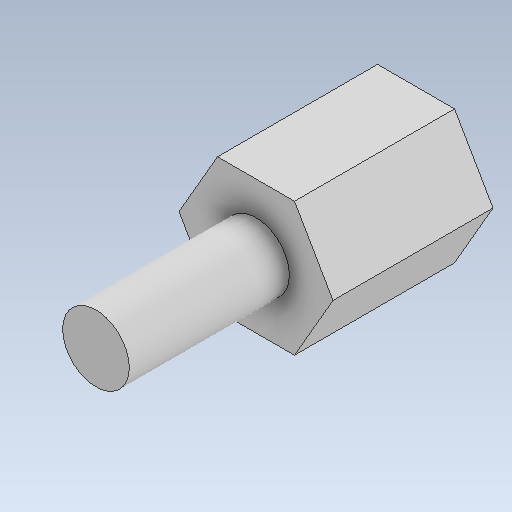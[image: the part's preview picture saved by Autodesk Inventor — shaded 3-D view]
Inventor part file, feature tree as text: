
AUTODESK INVENTOR PART (.ipt)
format: ipt  version: 2021 (Build 250183000, 183)  size: 114,688 bytes
history: native  units: mm
features: extrude x4, sketch x4, projected_geometry x1
ambient origin geometry x8: Origin, YZ Plane, XZ Plane, XY Plane, X Axis, Y Axis, Z Axis, Center Point
bodies: Solid1 (feature_tree)
feature tree (9):
  extrude  "Extrusion1"  Depth=6.0mm TaperAngle=0.0deg
  extrude  "Extrusion3"  Depth=7.0mm TaperAngle=0.0deg
  extrude  "Extrusion4"  Depth=6.0mm TaperAngle=0.0deg
  extrude  "Extrusion5"  [1 undecoded]
  sketch  "Sketch1"  dims[d0=5.0mm d1=6.0mm d2=0.0mm]
  sketch  "Sketch3"  dims[d6=2.5mm d7=7.0mm d8=0.0mm]
  sketch  "Sketch4"  dims[d9=2.5mm d10=6.0mm d11=0.0mm]
  sketch  "Sketch5"  dims[d12=3.0mm d13=0.0mm]
  projected_geometry  "Projected Loop1"
note: 1 required parameter value undecoded (feature->parameter linkage not recoverable at this tier; creation-order binding heuristic only, values carry confidence <= 0.55)
